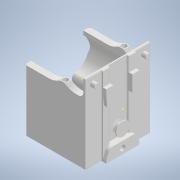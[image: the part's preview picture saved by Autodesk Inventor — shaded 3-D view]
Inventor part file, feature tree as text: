
AUTODESK INVENTOR PART (.ipt)
format: ipt  version: 2022 (Build 260153000, 153)  size: 798,208 bytes
history: native  units: mm
features: reference x24, sketch x23, extrude x21, projected_geometry x20, fillet x11, other x10, chamfer x1
ambient origin geometry x8: Origin, YZ Plane, XZ Plane, XY Plane, X Axis, Y Axis, Z Axis, Center Point
bodies: Body1 (feature_tree)
feature tree (110):
  other  "Твердое тело1"
  extrude  "Выдавливание1"  Depth=34.5mm TaperAngle=0.0deg
  extrude  "Выдавливание2"  Depth=0.5mm
  extrude  "Выдавливание3"  Depth=0.3mm
  extrude  "Выдавливание4"  Depth=5.0mm
  extrude  "Выдавливание5"  Depth=5.0mm
  extrude  "Выдавливание6"  Depth=5.0mm
  extrude  "Выдавливание8"  Depth=15.0mm
  extrude  "Выдавливание9"  Depth=15.0mm
  chamfer  "Фаска1"  Distance=15.0mm
  fillet  "Сопряжение1"  Radius=1.7mm
  extrude  "Выдавливание11"  Depth=2.0mm TaperAngle=0.0deg
  fillet  "Сопряжение4"  Radius=0.8mm
  fillet  "Сопряжение5"  Radius=4.7mm
  sketch  "Эскиз15"
  extrude  "Выдавливание12"  Depth=0.4mm
  sketch  "Эскиз17"
  extrude  "Выдавливание13"  Depth=0.4mm
  extrude  "Выдавливание14"  Depth=200.0mm TaperAngle=0.0deg
  fillet  "Сопряжение10"  Radius=0.5mm
  extrude  "Выдавливание18"  Depth=2.3mm TaperAngle=0.0deg
  extrude  "Выдавливание19"  Depth=10.0mm
  extrude  "Выдавливание20"  Depth=10.0mm
  extrude  "Выдавливание21"  Depth=3.0mm
  fillet  "Сопряжение13"  Radius=4.0mm
  fillet  "Сопряжение14"  Radius=3.0mm
  fillet  "Сопряжение15"  Radius=4.0mm
  extrude  "Выдавливание22"  Depth=2.3mm TaperAngle=0.0deg
  fillet  "Сопряжение16"  Radius=2.3mm
  extrude  "Выдавливание23"  Depth=10.0mm
  extrude  "Выдавливание24"  Depth=30.0mm
  fillet  "Сопряжение17"  Radius=0.8mm
  extrude  "Выдавливание25"  Depth=0.15mm
  fillet  "Сопряжение19"  Radius=3.0mm
  extrude  "Выдавливание26"  Depth=50.0mm TaperAngle=0.0deg
  fillet  "Сопряжение20"  Radius=4.0mm
  sketch  "Эскиз1"
  reference  "Ссылка1"
  reference  "Ссылка2"
  reference  "Ссылка3"
  reference  "Ссылка4"
  reference  "Ссылка5"
  reference  "Ссылка6"
  reference  "Ссылка7"
  reference  "Ссылка8"
  sketch  "Эскиз2"
  projected_geometry  "Спроецированная петля1"
  projected_geometry  "Спроецированная петля2"
  sketch  "Эскиз3"
  reference  "Ссылка9"
  reference  "Ссылка10"
  sketch  "Эскиз4"
  projected_geometry  "Спроецированная петля3"
  reference  "Ссылка11"
  reference  "Ссылка12"
  reference  "Ссылка13"
  reference  "Ссылка14"
  sketch  "Эскиз5"
  reference  "Ссылка15"
  reference  "Ссылка16"
  projected_geometry  "Спроецированная петля4"
  sketch  "Эскиз7"
  projected_geometry  "Спроецированная петля6"
  sketch  "Эскиз11"
  projected_geometry  "Спроецированная петля8"
  sketch  "Эскиз12"
  reference  "Ссылка27"
  sketch  "Эскиз14"
  sketch  "Эскиз16"
  reference  "Ссылка29"
  projected_geometry  "Спроецированная петля10"
  projected_geometry  "Спроецированная петля11"
  projected_geometry  "Спроецированная петля12"
  reference  "Ссылка30"
  reference  "Ссылка31"
  sketch  "Эскиз18"
  projected_geometry  "Спроецированная петля14"
  sketch  "Эскиз19"
  projected_geometry  "Спроецированная петля15"
  projected_geometry  "Спроецированная петля16"
  sketch  "Эскиз23"
  projected_geometry  "Спроецированная петля23"
  sketch  "Эскиз24"
  projected_geometry  "Спроецированная петля24"
  sketch  "Эскиз25"
  sketch  "Эскиз26"
  sketch  "Эскиз27"
  projected_geometry  "Спроецированная петля25"
  sketch  "Эскиз28"
  sketch  "Эскиз29"
  sketch  "Эскиз30"
  reference  "Ссылка32"
  projected_geometry  "Спроецированная петля26"
  projected_geometry  "Спроецированная петля27"
  reference  "Ссылка33"
  projected_geometry  "Спроецированная петля28"
  sketch  "Эскиз31"
  projected_geometry  "Спроецированная петля29"
  projected_geometry  "Спроецированная петля30"
  reference  "Ссылка34"
  reference  "Ссылка35"
  other  "<userpath>\OneDrive\Документы\Git\MZCAT_battery\FastBattery.iam"
  other  "FastBattery.iam"
  other  "plan:1"
  other  "BMS_board:1"
  other  "metal_body:1"
  other  "metal_cap:1"
  other  "<userpath>\Documents\Git\MZCAT_2024_construction\MZCAT_battery\FastBattery2.iam"
  other  "FastBattery2.iam"
  other  "metal_body_fixed:1"
